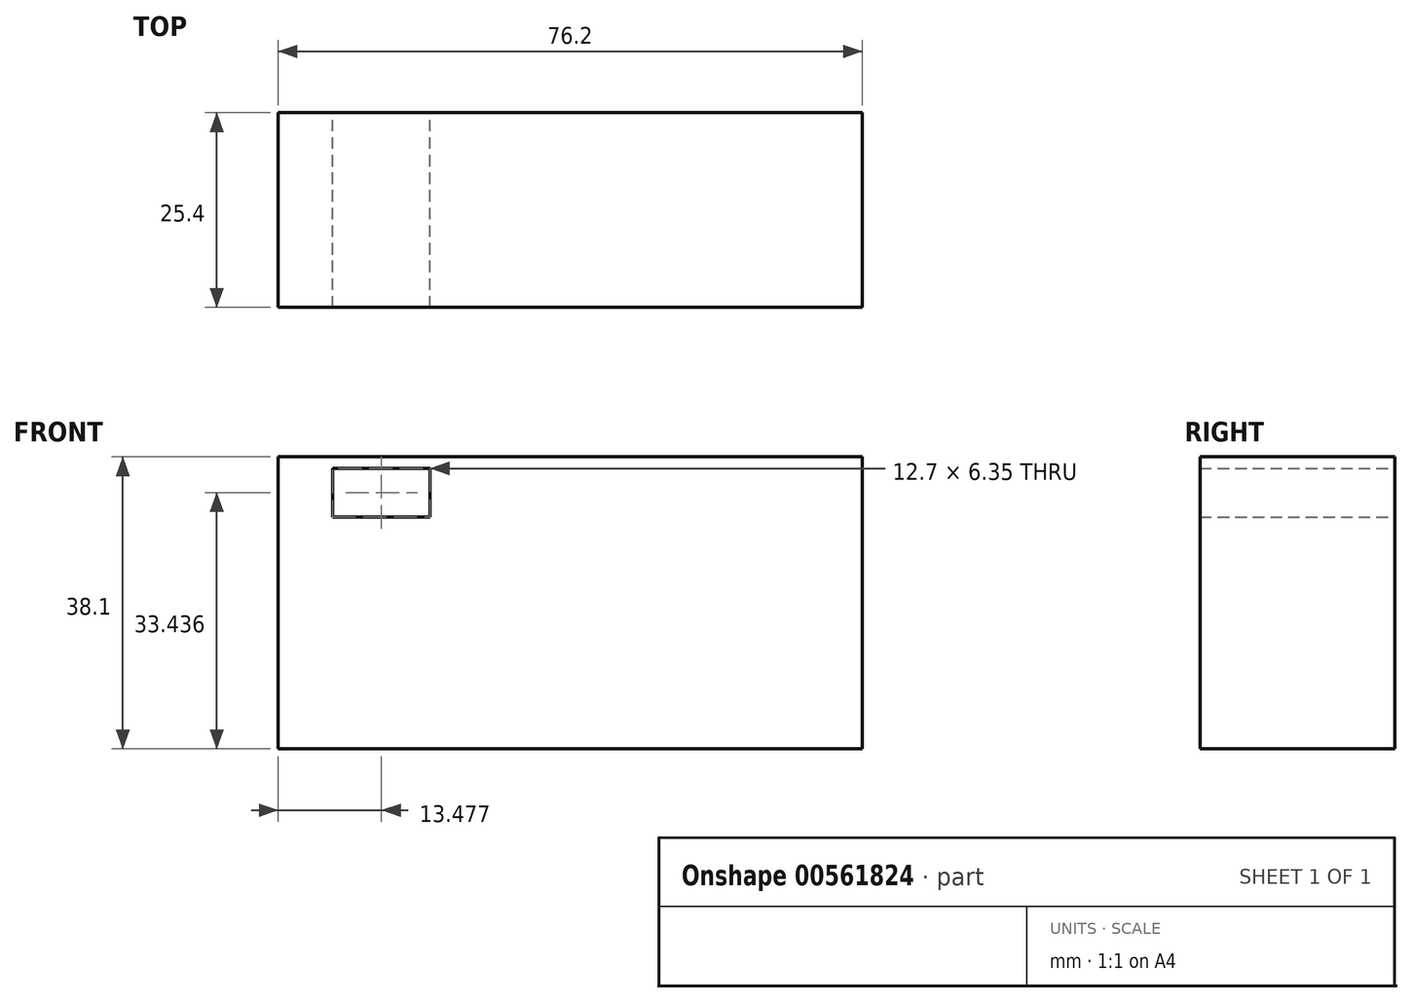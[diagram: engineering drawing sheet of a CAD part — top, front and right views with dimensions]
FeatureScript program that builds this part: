
annotation { "Feature Type Name" : "Feature", "Feature Type Description" : "" }
export const myFeature = defineFeature(function(context is Context, id is Id, definition is map)
    precondition{}
    {
        {
            var Q0;
            Q0=qCreatedBy(makeId("Front.planeOp"),FACE);
            var sketch = newSketch(context, id + "F0", { "sketchPlane" : qUnion([Q0])});
            skLineSegment(sketch, "E0.bottom", {"start": v(-38.1, 19.05) * mm, "end": v(38.1, 19.05) * mm});
            skLineSegment(sketch, "E0.top", {"start": v(-38.1, -19.05) * mm, "end": v(38.1, -19.05) * mm});
            skLineSegment(sketch, "E0.left", {"start": v(-38.1, 19.05) * mm, "end": v(-38.1, -19.05) * mm});
            skLineSegment(sketch, "E0.right", {"start": v(38.1, 19.05) * mm, "end": v(38.1, -19.05) * mm});
            skPoint(sketch, "E0.middle", {"position": v(0, 0) * mm});
            skSolve(sketch);
        }
        {
            var Q0;
            Q0 = qSketchRegion(id + "F0", true);
            extrude(context, id + "F1", {"entities" : qUnion([Q0]), "depth" : 25.4 * mm, "offsetDistance" : 25.4 * mm});
        }
        {
            var Q0;
            Q0=qCreatedBy(makeId("Front.planeOp"),FACE);
            var sketch = newSketch(context, id + "F2", { "sketchPlane" : qUnion([Q0])});
            skLineSegment(sketch, "E1.bottom", {"start": v(-21.98, 9.44) * mm, "end": v(-34.68, 9.44) * mm});
            skLineSegment(sketch, "E1.top", {"start": v(-21.98, 15.79) * mm, "end": v(-34.68, 15.79) * mm});
            skLineSegment(sketch, "E1.left", {"start": v(-21.98, 9.44) * mm, "end": v(-21.98, 15.79) * mm});
            skLineSegment(sketch, "E1.right", {"start": v(-34.68, 9.44) * mm, "end": v(-34.68, 15.79) * mm});
            skPoint(sketch, "E1.middle", {"position": v(-28.33, 12.61) * mm});
            skSolve(sketch);
        }
        {
            var Q0;
            Q0 = qSketchRegion(id + "F2", true);
            extrude(context, id + "F3", {"entities" : qUnion([Q0]), "operationType" : NewBodyOperationType.REMOVE, "oppositeDirection" : true, "depth" : 36.83 * mm, "offsetDistance" : 25.4 * mm});
        }
        {
            var Q0;
            Q0=qCreatedBy(makeId("Front.planeOp"),FACE);
            var sketch = newSketch(context, id + "F4", { "sketchPlane" : qUnion([Q0])});
            skLineSegment(sketch, "E2.bottom", {"start": v(-18.27, 11.21) * mm, "end": v(-30.97, 11.21) * mm});
            skLineSegment(sketch, "E2.top", {"start": v(-18.27, 17.56) * mm, "end": v(-30.97, 17.56) * mm});
            skLineSegment(sketch, "E2.left", {"start": v(-18.27, 11.21) * mm, "end": v(-18.27, 17.56) * mm});
            skLineSegment(sketch, "E2.right", {"start": v(-30.97, 11.21) * mm, "end": v(-30.97, 17.56) * mm});
            skPoint(sketch, "E2.middle", {"position": v(-24.62, 14.39) * mm});
            skSolve(sketch);
        }
        {
            var Q0;
            Q0 = qSketchRegion(id + "F4", true);
            extrude(context, id + "F5", {"entities" : qUnion([Q0]), "operationType" : NewBodyOperationType.REMOVE, "depth" : 101.85 * mm, "offsetDistance" : 25.4 * mm});
        }
    });
